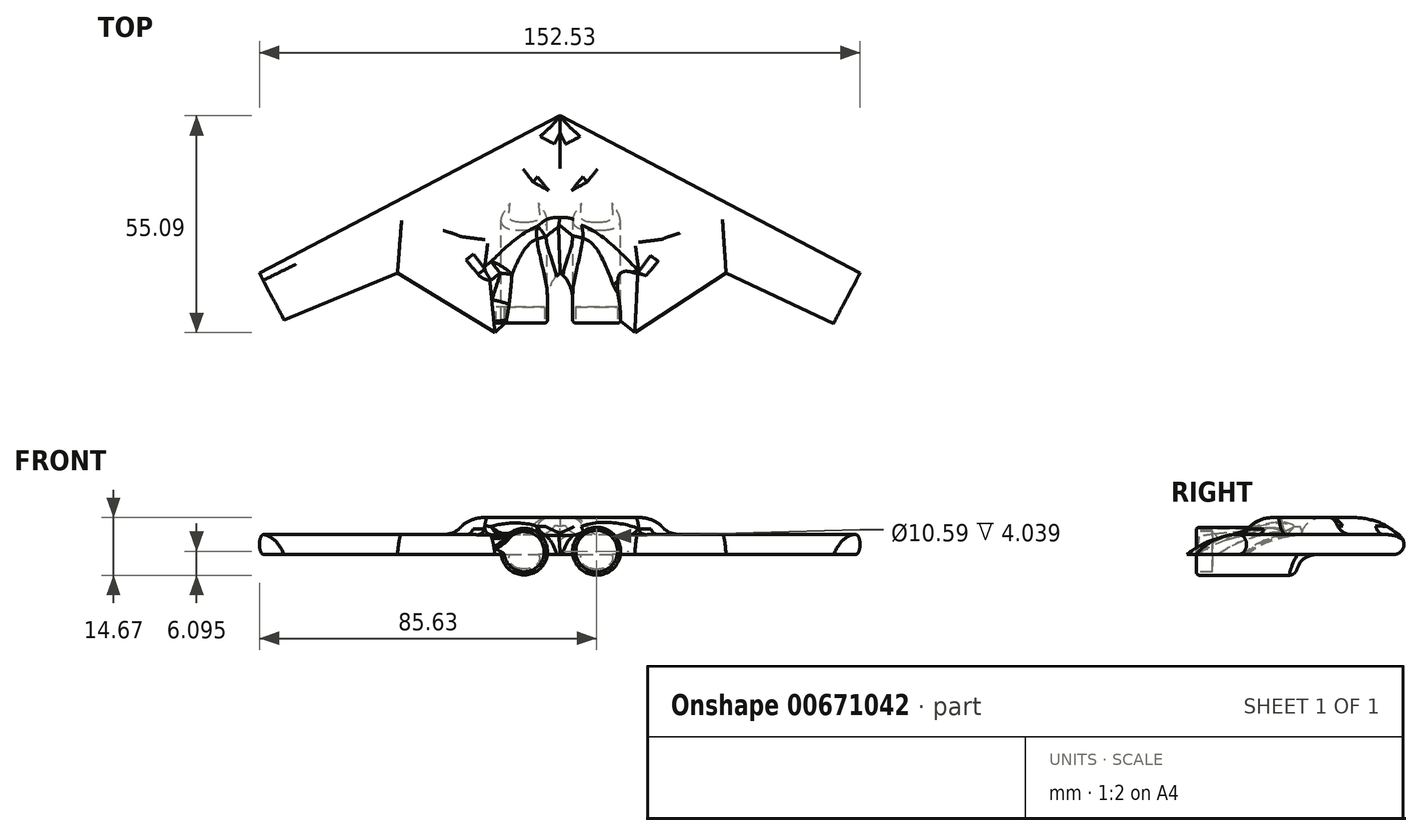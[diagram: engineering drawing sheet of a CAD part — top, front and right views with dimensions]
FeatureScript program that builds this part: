
annotation { "Feature Type Name" : "Feature", "Feature Type Description" : "" }
export const myFeature = defineFeature(function(context is Context, id is Id, definition is map)
    precondition{}
    {
        {
            var Q0;
            Q0=qCreatedBy(makeId("Top.planeOp"),FACE);
            var sketch = newSketch(context, id + "F0", { "sketchPlane" : qUnion([Q0])});
            skLineSegment(sketch, "E0", {"start": v(-76.35, 0) * mm, "end": v(0, 40) * mm});
            skLineSegment(sketch, "E1", {"start": v(0, 40) * mm, "end": v(76.18, 0) * mm});
            skLineSegment(sketch, "E2", {"start": v(76.18, 0) * mm, "end": v(69.47, -12.78) * mm});
            skLineSegment(sketch, "E3", {"start": v(-76.35, 0) * mm, "end": v(-70.12, -11.89) * mm});
            skLineSegment(sketch, "E4", {"start": v(-70.12, -11.89) * mm, "end": v(-41.31, 0) * mm});
            skLineSegment(sketch, "E5", {"start": v(-41.31, 0) * mm, "end": v(-16.56, -15.08) * mm});
            skLineSegment(sketch, "E6", {"start": v(-16.56, -15.08) * mm, "end": v(0, 0) * mm});
            skLineSegment(sketch, "E7", {"start": v(0, 0) * mm, "end": v(19, -15.08) * mm});
            skLineSegment(sketch, "E8", {"start": v(19, -15.08) * mm, "end": v(42.18, 0) * mm});
            skLineSegment(sketch, "E9", {"start": v(42.18, 0) * mm, "end": v(69.47, -12.78) * mm});
            skSolve(sketch);
        }
        {
            var Q0;
            Q0 = qSketchRegion(id + "F0", true);
            extrude(context, id + "F1", {"entities" : qUnion([Q0]), "endBound" : BoundingType.SYMMETRIC, "oppositeDirection" : true, "depth" : 5.08 * mm, "offsetDistance" : 25.4 * mm});
        }
        {
            var Q0;
            Q0=makeQuery(id+"F1.opExtrude","CAP_EDGE",EDGE,{"disambiguationData":[OSD([sQuery(id+"F0.wireOp",EDGE,"E1")])],"isStart":true});
            var Q1;
            Q1=makeQuery(id+"F1.opExtrude","CAP_EDGE",EDGE,{"disambiguationData":[OSD([sQuery(id+"F0.wireOp",EDGE,"E0")])],"isStart":true});
            var Q2;
            Q2=makeQuery(id+"F1.opExtrude","CAP_EDGE",EDGE,{"disambiguationData":[OSD([sQuery(id+"F0.wireOp",EDGE,"E1")])],"isStart":false});
            var Q3;
            Q3=makeQuery(id+"F1.opExtrude","CAP_EDGE",EDGE,{"disambiguationData":[OSD([sQuery(id+"F0.wireOp",EDGE,"E0")])],"isStart":false});
            fillet(context, id + "F2", {"entities" : qUnion([Q0, Q1, Q2, Q3]), "radius" : 2.3 * mm, "tangentPropagation" : true, "allowEdgeOverflow" : false});
        }
        {
            var Q0;
            Q0=makeQuery(id+"F1.opExtrude","CAP_EDGE",EDGE,{"disambiguationData":[OSD([sQuery(id+"F0.wireOp",EDGE,"E4")])],"isStart":true});
            var Q1;
            Q1=makeQuery(id+"F1.opExtrude","CAP_EDGE",EDGE,{"disambiguationData":[OSD([sQuery(id+"F0.wireOp",EDGE,"E5")])],"isStart":true});
            var Q2;
            Q2=makeQuery(id+"F1.opExtrude","CAP_EDGE",EDGE,{"disambiguationData":[OSD([sQuery(id+"F0.wireOp",EDGE,"E6")])],"isStart":true});
            var Q3;
            Q3=makeQuery(id+"F1.opExtrude","CAP_EDGE",EDGE,{"disambiguationData":[OSD([sQuery(id+"F0.wireOp",EDGE,"E7")])],"isStart":true});
            var Q4;
            Q4=makeQuery(id+"F1.opExtrude","CAP_EDGE",EDGE,{"disambiguationData":[OSD([sQuery(id+"F0.wireOp",EDGE,"E8")])],"isStart":true});
            var Q5;
            Q5=makeQuery(id+"F1.opExtrude","CAP_EDGE",EDGE,{"disambiguationData":[OSD([sQuery(id+"F0.wireOp",EDGE,"E9")])],"isStart":true});
            fillet(context, id + "F3", {"entities" : qUnion([Q0, Q1, Q2, Q3, Q4, Q5]), "radius" : 16.56 * mm, "tangentPropagation" : true, "allowEdgeOverflow" : false});
        }
        {
            var Q0;
            Q0=qCreatedBy(makeId("Top.planeOp"),FACE);
            var sketch = newSketch(context, id + "F4", { "sketchPlane" : qUnion([Q0])});
            skLineSegment(sketch, "E10", {"start": v(0, 37.4) * mm, "end": v(-6.87, 24.32) * mm});
            skLineSegment(sketch, "E11", {"start": v(-6.87, 24.32) * mm, "end": v(0, 15.43) * mm});
            skLineSegment(sketch, "E12", {"start": v(0, 15.43) * mm, "end": v(6.9, 24.32) * mm});
            skLineSegment(sketch, "E13", {"start": v(6.9, 24.32) * mm, "end": v(0, 37.4) * mm});
            skSolve(sketch);
        }
        {
            var Q0;
            Q0 = qSketchRegion(id + "F4", true);
            extrude(context, id + "F5", {"entities" : qUnion([Q0]), "operationType" : NewBodyOperationType.ADD, "depth" : 6.86 * mm, "offsetDistance" : 25.4 * mm});
        }
        {
            var Q0;
            Q0=makeQuery(id+"F5.opExtrude","SWEPT_FACE",FACE,{"disambiguationData":[OSD([sQuery(id+"F4.wireOp",EDGE,"E12")])]});
            extrude(context, id + "F6", {"entities" : qUnion([Q0]), "operationType" : NewBodyOperationType.ADD, "depth" : 25.4 * mm, "offsetDistance" : 25.4 * mm});
        }
        {
            var Q0;
            Q0=makeQuery(id+"F5.opExtrude","SWEPT_FACE",FACE,{"disambiguationData":[OSD([sQuery(id+"F4.wireOp",EDGE,"E11")])]});
            extrude(context, id + "F7", {"entities" : qUnion([Q0]), "operationType" : NewBodyOperationType.ADD, "depth" : 24.38 * mm, "offsetDistance" : 25.4 * mm});
        }
        {
            var Q0;
            Q0=makeQuery(id+"F7.opExtrude","SWEPT_EDGE",EDGE,{"disambiguationData":[OSD([sQuery(id+"F4.wireOp",EDGE,"E10"),sQuery(id+"F4.wireOp",EDGE,"E11")])]});
            var Q1;
            Q1=makeQuery(id+"F6.opExtrude","SWEPT_EDGE",EDGE,{"disambiguationData":[OSD([sQuery(id+"F4.wireOp",EDGE,"E12"),sQuery(id+"F4.wireOp",EDGE,"E13")])]});
            var Q2;
            {var subQ0=sQuery(id+"F4.wireOp",EDGE,"E12");var subQ1=sQuery(id+"F4.wireOp",EDGE,"E11");Q2=makeQuery(id+"F7.boolean.opBoolean","MERGE",EDGE,{"derivedFrom":[makeQuery(id+"F6.boolean.opBoolean","MERGE",EDGE,{"derivedFrom":[makeQuery(id+"F5.opExtrude","SWEPT_EDGE",EDGE,{"disambiguationData":[OSD([subQ1,subQ0])]}),makeQuery(id+"F6.opExtrude","CAP_EDGE",EDGE,{"disambiguationData":[OSD([subQ1,subQ0])],"isStart":true})]}),makeQuery(id+"F7.opExtrude","CAP_EDGE",EDGE,{"disambiguationData":[OSD([subQ1,subQ0])],"isStart":true})]});}
            fillet(context, id + "F8", {"entities" : qUnion([Q0, Q1, Q2]), "radius" : 5.08 * mm, "tangentPropagation" : true, "allowEdgeOverflow" : false});
        }
        {
            var Q0;
            {var subQ0=sQuery(id+"F4.wireOp",EDGE,"E11");Q0=makeQuery(id+"F8.opFillet","BLEND_EDGE",EDGE,{"blendedFrom":[makeQuery(id+"F7.opExtrude","SWEPT_EDGE",EDGE,{"disambiguationData":[OSD([sQuery(id+"F4.wireOp",EDGE,"E10"),subQ0])]}),makeQuery(id+"F7.opExtrude","CAP_FACE",FACE,{"disambiguationData":[OSD([subQ0])],"isStart":false})],"blendedInto":[makeQuery(id+"F7.opExtrude","CAP_FACE",FACE,{"disambiguationData":[OSD([subQ0])],"isStart":false})]});}
            var Q1;
            Q1=makeQuery(id+"F6.opExtrude","CAP_EDGE",EDGE,{"disambiguationData":[OSD([sQuery(id+"F4.wireOp",EDGE,"E12")])],"isStart":false});
            fillet(context, id + "F9", {"entities" : qUnion([Q0, Q1]), "radius" : 5.08 * mm, "tangentPropagation" : true, "allowEdgeOverflow" : false});
        }
        {
            var Q0;
            Q0=makeQuery(id+"F5.opExtrude","CAP_EDGE",EDGE,{"disambiguationData":[OSD([sQuery(id+"F4.wireOp",EDGE,"E13")])],"isStart":false});
            var Q1;
            Q1=makeQuery(id+"F5.opExtrude","CAP_EDGE",EDGE,{"disambiguationData":[OSD([sQuery(id+"F4.wireOp",EDGE,"E10")])],"isStart":false});
            fillet(context, id + "F10", {"entities" : qUnion([Q0, Q1]), "radius" : 5.08 * mm, "tangentPropagation" : true, "allowEdgeOverflow" : false});
        }
        {
            var Q0;
            {var subQ0=sQuery(id+"F4.wireOp",EDGE,"E11");var subQ1=sQuery(id+"F4.wireOp",EDGE,"E12");Q0=makeQuery(id+"F8.opFillet","BLEND_EDGE",EDGE,{"blendedFrom":[makeQuery(id+"F7.boolean.opBoolean","MERGE",EDGE,{"derivedFrom":[makeQuery(id+"F6.boolean.opBoolean","MERGE",EDGE,{"derivedFrom":[makeQuery(id+"F5.opExtrude","SWEPT_EDGE",EDGE,{"disambiguationData":[OSD([subQ0,subQ1])]}),makeQuery(id+"F6.opExtrude","CAP_EDGE",EDGE,{"disambiguationData":[OSD([subQ0,subQ1])],"isStart":true})]}),makeQuery(id+"F7.opExtrude","CAP_EDGE",EDGE,{"disambiguationData":[OSD([subQ0,subQ1])],"isStart":true})]}),makeQuery(id+"F7.boolean.opBoolean","MERGE",FACE,{"derivedFrom":[makeQuery(id+"F6.boolean.opBoolean","MERGE",FACE,{"derivedFrom":[makeQuery(id+"F5.opExtrude","CAP_FACE",FACE,{"disambiguationData":[OSD([sQuery(id+"F4.wireOp",EDGE,"E10"),subQ0,subQ1,sQuery(id+"F4.wireOp",EDGE,"E13")])],"isStart":false}),makeQuery(id+"F6.opExtrude","SWEPT_FACE",FACE,{"disambiguationData":[OSD([subQ1])]})]}),makeQuery(id+"F7.opExtrude","SWEPT_FACE",FACE,{"disambiguationData":[OSD([subQ0])]})]})],"blendedInto":[makeQuery(id+"F7.boolean.opBoolean","MERGE",FACE,{"derivedFrom":[makeQuery(id+"F6.boolean.opBoolean","MERGE",FACE,{"derivedFrom":[makeQuery(id+"F5.opExtrude","CAP_FACE",FACE,{"disambiguationData":[OSD([sQuery(id+"F4.wireOp",EDGE,"E10"),subQ0,subQ1,sQuery(id+"F4.wireOp",EDGE,"E13")])],"isStart":false}),makeQuery(id+"F6.opExtrude","SWEPT_FACE",FACE,{"disambiguationData":[OSD([subQ1])]})]}),makeQuery(id+"F7.opExtrude","SWEPT_FACE",FACE,{"disambiguationData":[OSD([subQ0])]})]})]});}
            fillet(context, id + "F11", {"entities" : qUnion([Q0]), "radius" : 5.08 * mm, "tangentPropagation" : true, "allowEdgeOverflow" : false});
        }
        {
            var Q0;
            Q0=qCreatedBy(makeId("Front.planeOp"),FACE);
            var sketch = newSketch(context, id + "F12", { "sketchPlane" : qUnion([Q0])});
            skCircle(sketch, "E14", {"center": v(-9.12, -1.82) * mm, "radius": 5.9 * mm});
            skCircle(sketch, "E15", {"center": v(9.28, -1.72) * mm, "radius": 6.1 * mm});
            skSolve(sketch);
        }
        {
            var Q0;
            Q0 = qSketchRegion(id + "F12", true);
            extrude(context, id + "F13", {"entities" : qUnion([Q0]), "operationType" : NewBodyOperationType.ADD, "endBound" : BoundingType.SYMMETRIC, "depth" : 25.4 * mm, "offsetDistance" : 25.4 * mm});
        }
        {
            var Q0;
            Q0=makeQuery(id+"F13.boolean.opBoolean","INTERSECT",EDGE,{"derivedFrom":[makeQuery(id+"F1.opExtrude","CAP_FACE",FACE,{"disambiguationData":[OSD([sQuery(id+"F0.wireOp",EDGE,"E0"),sQuery(id+"F0.wireOp",EDGE,"E1"),sQuery(id+"F0.wireOp",EDGE,"E2"),sQuery(id+"F0.wireOp",EDGE,"E3"),sQuery(id+"F0.wireOp",EDGE,"E4"),sQuery(id+"F0.wireOp",EDGE,"E5"),sQuery(id+"F0.wireOp",EDGE,"E6"),sQuery(id+"F0.wireOp",EDGE,"E7"),sQuery(id+"F0.wireOp",EDGE,"E8"),sQuery(id+"F0.wireOp",EDGE,"E9")])],"isStart":false}),makeQuery(id+"F13.opExtrude","CAP_FACE",FACE,{"disambiguationData":[OSD([sQuery(id+"F12.wireOp",EDGE,"E15")])],"isStart":true})]});
            var Q1;
            Q1=makeQuery(id+"F13.boolean.opBoolean","INTERSECT",EDGE,{"derivedFrom":[makeQuery(id+"F1.opExtrude","CAP_FACE",FACE,{"disambiguationData":[OSD([sQuery(id+"F0.wireOp",EDGE,"E0"),sQuery(id+"F0.wireOp",EDGE,"E1"),sQuery(id+"F0.wireOp",EDGE,"E2"),sQuery(id+"F0.wireOp",EDGE,"E3"),sQuery(id+"F0.wireOp",EDGE,"E4"),sQuery(id+"F0.wireOp",EDGE,"E5"),sQuery(id+"F0.wireOp",EDGE,"E6"),sQuery(id+"F0.wireOp",EDGE,"E7"),sQuery(id+"F0.wireOp",EDGE,"E8"),sQuery(id+"F0.wireOp",EDGE,"E9")])],"isStart":false}),makeQuery(id+"F13.opExtrude","CAP_FACE",FACE,{"disambiguationData":[OSD([sQuery(id+"F12.wireOp",EDGE,"E14")])],"isStart":true})]});
            fillet(context, id + "F14", {"entities" : qUnion([Q0, Q1]), "radius" : 5.08 * mm, "tangentPropagation" : true, "allowEdgeOverflow" : false});
        }
        {
            var Q0;
            {var subQ0=sQuery(id+"F12.wireOp",EDGE,"E14");Q0=makeQuery(id+"F14.opFillet","BLEND_EDGE",EDGE,{"disambiguationData":[OD(0.0)],"blendedFrom":[makeQuery(id+"F13.boolean.opBoolean","INTERSECT",EDGE,{"derivedFrom":[makeQuery(id+"F1.opExtrude","CAP_FACE",FACE,{"disambiguationData":[OSD([sQuery(id+"F0.wireOp",EDGE,"E0"),sQuery(id+"F0.wireOp",EDGE,"E1"),sQuery(id+"F0.wireOp",EDGE,"E2"),sQuery(id+"F0.wireOp",EDGE,"E3"),sQuery(id+"F0.wireOp",EDGE,"E4"),sQuery(id+"F0.wireOp",EDGE,"E5"),sQuery(id+"F0.wireOp",EDGE,"E6"),sQuery(id+"F0.wireOp",EDGE,"E7"),sQuery(id+"F0.wireOp",EDGE,"E8"),sQuery(id+"F0.wireOp",EDGE,"E9")])],"isStart":false}),makeQuery(id+"F13.opExtrude","CAP_FACE",FACE,{"disambiguationData":[OSD([subQ0])],"isStart":true})]}),makeQuery(id+"F13.opExtrude","SWEPT_FACE",FACE,{"disambiguationData":[OSD([subQ0])]})],"blendedInto":[makeQuery(id+"F13.opExtrude","SWEPT_FACE",FACE,{"disambiguationData":[OSD([subQ0])]})]});}
            var Q1;
            Q1=makeQuery(id+"F14.opFillet","BLEND_FACE",FACE,{"disambiguationData":[OSD([sQuery(id+"F0.wireOp",EDGE,"E0"),sQuery(id+"F0.wireOp",EDGE,"E1"),sQuery(id+"F0.wireOp",EDGE,"E2"),sQuery(id+"F0.wireOp",EDGE,"E3"),sQuery(id+"F0.wireOp",EDGE,"E4"),sQuery(id+"F0.wireOp",EDGE,"E5"),sQuery(id+"F0.wireOp",EDGE,"E6"),sQuery(id+"F0.wireOp",EDGE,"E7"),sQuery(id+"F0.wireOp",EDGE,"E8"),sQuery(id+"F0.wireOp",EDGE,"E9"),sQuery(id+"F12.wireOp",EDGE,"E15")])]});
            var Q2;
            Q2=makeQuery(id+"F14.opFillet","BLEND_FACE",FACE,{"disambiguationData":[OSD([sQuery(id+"F0.wireOp",EDGE,"E0"),sQuery(id+"F0.wireOp",EDGE,"E1"),sQuery(id+"F0.wireOp",EDGE,"E2"),sQuery(id+"F0.wireOp",EDGE,"E3"),sQuery(id+"F0.wireOp",EDGE,"E4"),sQuery(id+"F0.wireOp",EDGE,"E5"),sQuery(id+"F0.wireOp",EDGE,"E6"),sQuery(id+"F0.wireOp",EDGE,"E7"),sQuery(id+"F0.wireOp",EDGE,"E8"),sQuery(id+"F0.wireOp",EDGE,"E9"),sQuery(id+"F12.wireOp",EDGE,"E14")])]});
            fillet(context, id + "F15", {"entities" : qUnion([Q0, Q1, Q2]), "radius" : 2.03 * mm, "tangentPropagation" : true, "allowEdgeOverflow" : false});
        }
        {
            var Q0;
            {var subQ0=sQuery(id+"F4.wireOp",EDGE,"E12");var subQ1=sQuery(id+"F4.wireOp",EDGE,"E11");Q0=makeQuery(id+"F13.boolean.opBoolean","INTERSECT",EDGE,{"derivedFrom":[makeQuery(id+"F11.opFillet","BLEND_FACE",FACE,{"disambiguationData":[OSD([subQ1,subQ0]),TDD([makeQuery(id+"F7.opExtrude","SWEPT_EDGE",EDGE,{"disambiguationData":[OSD([subQ1,subQ0])]})])]}),makeQuery(id+"F13.opExtrude","SWEPT_FACE",FACE,{"disambiguationData":[OSD([sQuery(id+"F12.wireOp",EDGE,"E14")])]})]});}
            var Q1;
            {var subQ0=sQuery(id+"F4.wireOp",EDGE,"E12");var subQ1=sQuery(id+"F4.wireOp",EDGE,"E11");Q1=makeQuery(id+"F13.boolean.opBoolean","INTERSECT",EDGE,{"derivedFrom":[makeQuery(id+"F11.opFillet","BLEND_FACE",FACE,{"disambiguationData":[OSD([subQ1,subQ0]),TDD([makeQuery(id+"F6.opExtrude","SWEPT_EDGE",EDGE,{"disambiguationData":[OSD([subQ1,subQ0])]})])]}),makeQuery(id+"F13.opExtrude","SWEPT_FACE",FACE,{"disambiguationData":[OSD([sQuery(id+"F12.wireOp",EDGE,"E15")])]})]});}
            fillet(context, id + "F16", {"entities" : qUnion([Q0, Q1]), "radius" : 5.08 * mm, "tangentPropagation" : true, "allowEdgeOverflow" : false});
        }
        {
            var Q0;
            Q0=makeQuery(id+"F13.boolean.opBoolean","INTERSECT",EDGE,{"disambiguationData":[OD(1.0)],"derivedFrom":[makeQuery(id+"F3.opFillet","BLEND_FACE",FACE,{"disambiguationData":[OSD([sQuery(id+"F0.wireOp",EDGE,"E6")])]}),makeQuery(id+"F13.opExtrude","SWEPT_FACE",FACE,{"disambiguationData":[OSD([sQuery(id+"F12.wireOp",EDGE,"E14")])]})]});
            var Q1;
            Q1=makeQuery(id+"F13.boolean.opBoolean","INTERSECT",EDGE,{"disambiguationData":[OD(1.0)],"derivedFrom":[makeQuery(id+"F3.opFillet","BLEND_FACE",FACE,{"disambiguationData":[OSD([sQuery(id+"F0.wireOp",EDGE,"E7")])]}),makeQuery(id+"F13.opExtrude","SWEPT_FACE",FACE,{"disambiguationData":[OSD([sQuery(id+"F12.wireOp",EDGE,"E15")])]})]});
            fillet(context, id + "F17", {"entities" : qUnion([Q0, Q1]), "radius" : 5.08 * mm, "tangentPropagation" : true, "allowEdgeOverflow" : false});
        }
        {
            var Q0;
            Q0=makeQuery(id+"F13.opExtrude","CAP_EDGE",EDGE,{"disambiguationData":[OSD([sQuery(id+"F12.wireOp",EDGE,"E14")])],"isStart":false});
            var Q1;
            Q1=makeQuery(id+"F13.opExtrude","CAP_EDGE",EDGE,{"disambiguationData":[OSD([sQuery(id+"F12.wireOp",EDGE,"E15")])],"isStart":false});
            fillet(context, id + "F18", {"entities" : qUnion([Q0, Q1]), "radius" : 0.8 * mm, "tangentPropagation" : true, "allowEdgeOverflow" : false});
        }
        {
            var Q0;
            Q0=makeQuery(id+"F13.opExtrude","CAP_FACE",FACE,{"disambiguationData":[OSD([sQuery(id+"F12.wireOp",EDGE,"E14")])],"isStart":false});
            var Q1;
            Q1=makeQuery(id+"F13.opExtrude","CAP_FACE",FACE,{"disambiguationData":[OSD([sQuery(id+"F12.wireOp",EDGE,"E15")])],"isStart":false});
            extrude(context, id + "F19", {"entities" : qUnion([Q0, Q1]), "operationType" : NewBodyOperationType.REMOVE, "oppositeDirection" : true, "depth" : 4.04 * mm, "offsetDistance" : 25.4 * mm});
        }
        {
            var Q0;
            {var subQ0=sQuery(id+"F4.wireOp",EDGE,"E13");var subQ1=sQuery(id+"F0.wireOp",EDGE,"E2");var subQ2=sQuery(id+"F0.wireOp",EDGE,"E9");var subQ3=sQuery(id+"F0.wireOp",EDGE,"E8");var subQ5=sQuery(id+"F4.wireOp",EDGE,"E12");var subQ6=sQuery(id+"F0.wireOp",EDGE,"E7");var subQ7=sQuery(id+"F0.wireOp",EDGE,"E5");var subQ8=sQuery(id+"F0.wireOp",EDGE,"E0");var subQ9=sQuery(id+"F0.wireOp",EDGE,"E1");var subQ10=sQuery(id+"F0.wireOp",EDGE,"E4");var subQ12=sQuery(id+"F0.wireOp",EDGE,"E6");var subQ13=sQuery(id+"F0.wireOp",EDGE,"E3");Q0=makeQuery(id+"F8.opFillet","BLEND_EDGE",EDGE,{"blendedFrom":[makeQuery(id+"F6.opExtrude","SWEPT_EDGE",EDGE,{"disambiguationData":[OSD([subQ5,subQ0])]}),makeQuery(id+"F7.boolean.opBoolean","SPLIT",FACE,{"disambiguationData":[TD([makeQuery(id+"F1.opExtrude","SWEPT_FACE",FACE,{"disambiguationData":[OSD([subQ1])]})])],"derivedFrom":makeQuery(id+"F1.opExtrude","CAP_FACE",FACE,{"disambiguationData":[OSD([subQ8,subQ9,subQ1,subQ13,subQ10,subQ7,subQ12,subQ6,subQ3,subQ2])],"isStart":true})})],"blendedInto":[makeQuery(id+"F7.boolean.opBoolean","SPLIT",FACE,{"disambiguationData":[TD([makeQuery(id+"F1.opExtrude","SWEPT_FACE",FACE,{"disambiguationData":[OSD([subQ1])]})])],"derivedFrom":makeQuery(id+"F1.opExtrude","CAP_FACE",FACE,{"disambiguationData":[OSD([subQ8,subQ9,subQ1,subQ13,subQ10,subQ7,subQ12,subQ6,subQ3,subQ2])],"isStart":true})})]});}
            var Q1;
            {var subQ1=sQuery(id+"F0.wireOp",EDGE,"E2");var subQ2=sQuery(id+"F0.wireOp",EDGE,"E9");var subQ3=sQuery(id+"F0.wireOp",EDGE,"E8");var subQ4=sQuery(id+"F4.wireOp",EDGE,"E10");var subQ6=sQuery(id+"F0.wireOp",EDGE,"E7");var subQ7=sQuery(id+"F0.wireOp",EDGE,"E5");var subQ8=sQuery(id+"F0.wireOp",EDGE,"E0");var subQ9=sQuery(id+"F0.wireOp",EDGE,"E1");var subQ10=sQuery(id+"F0.wireOp",EDGE,"E4");var subQ11=sQuery(id+"F4.wireOp",EDGE,"E11");var subQ12=sQuery(id+"F0.wireOp",EDGE,"E6");var subQ13=sQuery(id+"F0.wireOp",EDGE,"E3");Q1=makeQuery(id+"F8.opFillet","BLEND_EDGE",EDGE,{"blendedFrom":[makeQuery(id+"F7.opExtrude","SWEPT_EDGE",EDGE,{"disambiguationData":[OSD([subQ4,subQ11])]}),makeQuery(id+"F7.boolean.opBoolean","SPLIT",FACE,{"disambiguationData":[TD([makeQuery(id+"F1.opExtrude","SWEPT_FACE",FACE,{"disambiguationData":[OSD([subQ1])]})])],"derivedFrom":makeQuery(id+"F1.opExtrude","CAP_FACE",FACE,{"disambiguationData":[OSD([subQ8,subQ9,subQ1,subQ13,subQ10,subQ7,subQ12,subQ6,subQ3,subQ2])],"isStart":true})})],"blendedInto":[makeQuery(id+"F7.boolean.opBoolean","SPLIT",FACE,{"disambiguationData":[TD([makeQuery(id+"F1.opExtrude","SWEPT_FACE",FACE,{"disambiguationData":[OSD([subQ1])]})])],"derivedFrom":makeQuery(id+"F1.opExtrude","CAP_FACE",FACE,{"disambiguationData":[OSD([subQ8,subQ9,subQ1,subQ13,subQ10,subQ7,subQ12,subQ6,subQ3,subQ2])],"isStart":true})})]});}
            fillet(context, id + "F20", {"entities" : qUnion([Q0, Q1]), "radius" : 5.08 * mm, "tangentPropagation" : true, "allowEdgeOverflow" : false});
        }
        {
            var Q0;
            {var subQ0=sQuery(id+"F4.wireOp",EDGE,"E13");var subQ1=sQuery(id+"F0.wireOp",EDGE,"E2");var subQ2=sQuery(id+"F0.wireOp",EDGE,"E9");var subQ3=sQuery(id+"F0.wireOp",EDGE,"E8");var subQ6=sQuery(id+"F0.wireOp",EDGE,"E7");var subQ7=sQuery(id+"F0.wireOp",EDGE,"E5");var subQ8=sQuery(id+"F0.wireOp",EDGE,"E0");var subQ9=sQuery(id+"F0.wireOp",EDGE,"E1");var subQ10=sQuery(id+"F0.wireOp",EDGE,"E4");var subQ12=sQuery(id+"F0.wireOp",EDGE,"E6");var subQ13=sQuery(id+"F0.wireOp",EDGE,"E3");Q0=makeQuery(id+"F10.opFillet","BLEND_EDGE",EDGE,{"blendedFrom":[makeQuery(id+"F5.opExtrude","CAP_EDGE",EDGE,{"disambiguationData":[OSD([subQ0])],"isStart":false}),makeQuery(id+"F7.boolean.opBoolean","SPLIT",FACE,{"disambiguationData":[TD([makeQuery(id+"F1.opExtrude","SWEPT_FACE",FACE,{"disambiguationData":[OSD([subQ1])]})])],"derivedFrom":makeQuery(id+"F1.opExtrude","CAP_FACE",FACE,{"disambiguationData":[OSD([subQ8,subQ9,subQ1,subQ13,subQ10,subQ7,subQ12,subQ6,subQ3,subQ2])],"isStart":true})})],"blendedInto":[makeQuery(id+"F7.boolean.opBoolean","SPLIT",FACE,{"disambiguationData":[TD([makeQuery(id+"F1.opExtrude","SWEPT_FACE",FACE,{"disambiguationData":[OSD([subQ1])]})])],"derivedFrom":makeQuery(id+"F1.opExtrude","CAP_FACE",FACE,{"disambiguationData":[OSD([subQ8,subQ9,subQ1,subQ13,subQ10,subQ7,subQ12,subQ6,subQ3,subQ2])],"isStart":true})})]});}
            var Q1;
            {var subQ1=sQuery(id+"F0.wireOp",EDGE,"E2");var subQ2=sQuery(id+"F0.wireOp",EDGE,"E9");var subQ3=sQuery(id+"F0.wireOp",EDGE,"E8");var subQ4=sQuery(id+"F4.wireOp",EDGE,"E10");var subQ6=sQuery(id+"F0.wireOp",EDGE,"E7");var subQ7=sQuery(id+"F0.wireOp",EDGE,"E5");var subQ8=sQuery(id+"F0.wireOp",EDGE,"E0");var subQ9=sQuery(id+"F0.wireOp",EDGE,"E1");var subQ10=sQuery(id+"F0.wireOp",EDGE,"E4");var subQ12=sQuery(id+"F0.wireOp",EDGE,"E6");var subQ13=sQuery(id+"F0.wireOp",EDGE,"E3");Q1=makeQuery(id+"F10.opFillet","BLEND_EDGE",EDGE,{"blendedFrom":[makeQuery(id+"F5.opExtrude","CAP_EDGE",EDGE,{"disambiguationData":[OSD([subQ4])],"isStart":false}),makeQuery(id+"F7.boolean.opBoolean","SPLIT",FACE,{"disambiguationData":[TD([makeQuery(id+"F1.opExtrude","SWEPT_FACE",FACE,{"disambiguationData":[OSD([subQ1])]})])],"derivedFrom":makeQuery(id+"F1.opExtrude","CAP_FACE",FACE,{"disambiguationData":[OSD([subQ8,subQ9,subQ1,subQ13,subQ10,subQ7,subQ12,subQ6,subQ3,subQ2])],"isStart":true})})],"blendedInto":[makeQuery(id+"F7.boolean.opBoolean","SPLIT",FACE,{"disambiguationData":[TD([makeQuery(id+"F1.opExtrude","SWEPT_FACE",FACE,{"disambiguationData":[OSD([subQ1])]})])],"derivedFrom":makeQuery(id+"F1.opExtrude","CAP_FACE",FACE,{"disambiguationData":[OSD([subQ8,subQ9,subQ1,subQ13,subQ10,subQ7,subQ12,subQ6,subQ3,subQ2])],"isStart":true})})]});}
            fillet(context, id + "F21", {"entities" : qUnion([Q0, Q1]), "radius" : 5.08 * mm, "tangentPropagation" : true, "allowEdgeOverflow" : false});
        }
        {
            var Q0;
            {var subQ1=sQuery(id+"F0.wireOp",EDGE,"E2");var subQ2=sQuery(id+"F0.wireOp",EDGE,"E9");var subQ3=sQuery(id+"F0.wireOp",EDGE,"E8");var subQ6=sQuery(id+"F0.wireOp",EDGE,"E7");var subQ7=sQuery(id+"F0.wireOp",EDGE,"E5");var subQ8=sQuery(id+"F0.wireOp",EDGE,"E0");var subQ9=sQuery(id+"F0.wireOp",EDGE,"E1");var subQ10=sQuery(id+"F0.wireOp",EDGE,"E4");var subQ11=sQuery(id+"F4.wireOp",EDGE,"E11");var subQ12=sQuery(id+"F0.wireOp",EDGE,"E6");var subQ13=sQuery(id+"F0.wireOp",EDGE,"E3");Q0=makeQuery(id+"F9.opFillet","BLEND_EDGE",EDGE,{"blendedFrom":[makeQuery(id+"F7.opExtrude","CAP_EDGE",EDGE,{"disambiguationData":[OSD([subQ11])],"isStart":false}),makeQuery(id+"F7.boolean.opBoolean","SPLIT",FACE,{"disambiguationData":[TD([makeQuery(id+"F1.opExtrude","SWEPT_FACE",FACE,{"disambiguationData":[OSD([subQ1])]})])],"derivedFrom":makeQuery(id+"F1.opExtrude","CAP_FACE",FACE,{"disambiguationData":[OSD([subQ8,subQ9,subQ1,subQ13,subQ10,subQ7,subQ12,subQ6,subQ3,subQ2])],"isStart":true})})],"blendedInto":[makeQuery(id+"F7.boolean.opBoolean","SPLIT",FACE,{"disambiguationData":[TD([makeQuery(id+"F1.opExtrude","SWEPT_FACE",FACE,{"disambiguationData":[OSD([subQ1])]})])],"derivedFrom":makeQuery(id+"F1.opExtrude","CAP_FACE",FACE,{"disambiguationData":[OSD([subQ8,subQ9,subQ1,subQ13,subQ10,subQ7,subQ12,subQ6,subQ3,subQ2])],"isStart":true})})]});}
            var Q1;
            {var subQ1=sQuery(id+"F0.wireOp",EDGE,"E2");var subQ2=sQuery(id+"F0.wireOp",EDGE,"E9");var subQ3=sQuery(id+"F0.wireOp",EDGE,"E8");var subQ5=sQuery(id+"F4.wireOp",EDGE,"E12");var subQ6=sQuery(id+"F0.wireOp",EDGE,"E7");var subQ7=sQuery(id+"F0.wireOp",EDGE,"E5");var subQ8=sQuery(id+"F0.wireOp",EDGE,"E0");var subQ9=sQuery(id+"F0.wireOp",EDGE,"E1");var subQ10=sQuery(id+"F0.wireOp",EDGE,"E4");var subQ12=sQuery(id+"F0.wireOp",EDGE,"E6");var subQ13=sQuery(id+"F0.wireOp",EDGE,"E3");Q1=makeQuery(id+"F9.opFillet","BLEND_EDGE",EDGE,{"blendedFrom":[makeQuery(id+"F6.opExtrude","CAP_EDGE",EDGE,{"disambiguationData":[OSD([subQ5])],"isStart":false}),makeQuery(id+"F7.boolean.opBoolean","SPLIT",FACE,{"disambiguationData":[TD([makeQuery(id+"F1.opExtrude","SWEPT_FACE",FACE,{"disambiguationData":[OSD([subQ1])]})])],"derivedFrom":makeQuery(id+"F1.opExtrude","CAP_FACE",FACE,{"disambiguationData":[OSD([subQ8,subQ9,subQ1,subQ13,subQ10,subQ7,subQ12,subQ6,subQ3,subQ2])],"isStart":true})})],"blendedInto":[makeQuery(id+"F7.boolean.opBoolean","SPLIT",FACE,{"disambiguationData":[TD([makeQuery(id+"F1.opExtrude","SWEPT_FACE",FACE,{"disambiguationData":[OSD([subQ1])]})])],"derivedFrom":makeQuery(id+"F1.opExtrude","CAP_FACE",FACE,{"disambiguationData":[OSD([subQ8,subQ9,subQ1,subQ13,subQ10,subQ7,subQ12,subQ6,subQ3,subQ2])],"isStart":true})})]});}
            fillet(context, id + "F22", {"entities" : qUnion([Q0, Q1]), "radius" : 2.63 * mm, "tangentPropagation" : true, "allowEdgeOverflow" : false});
        }
    });
